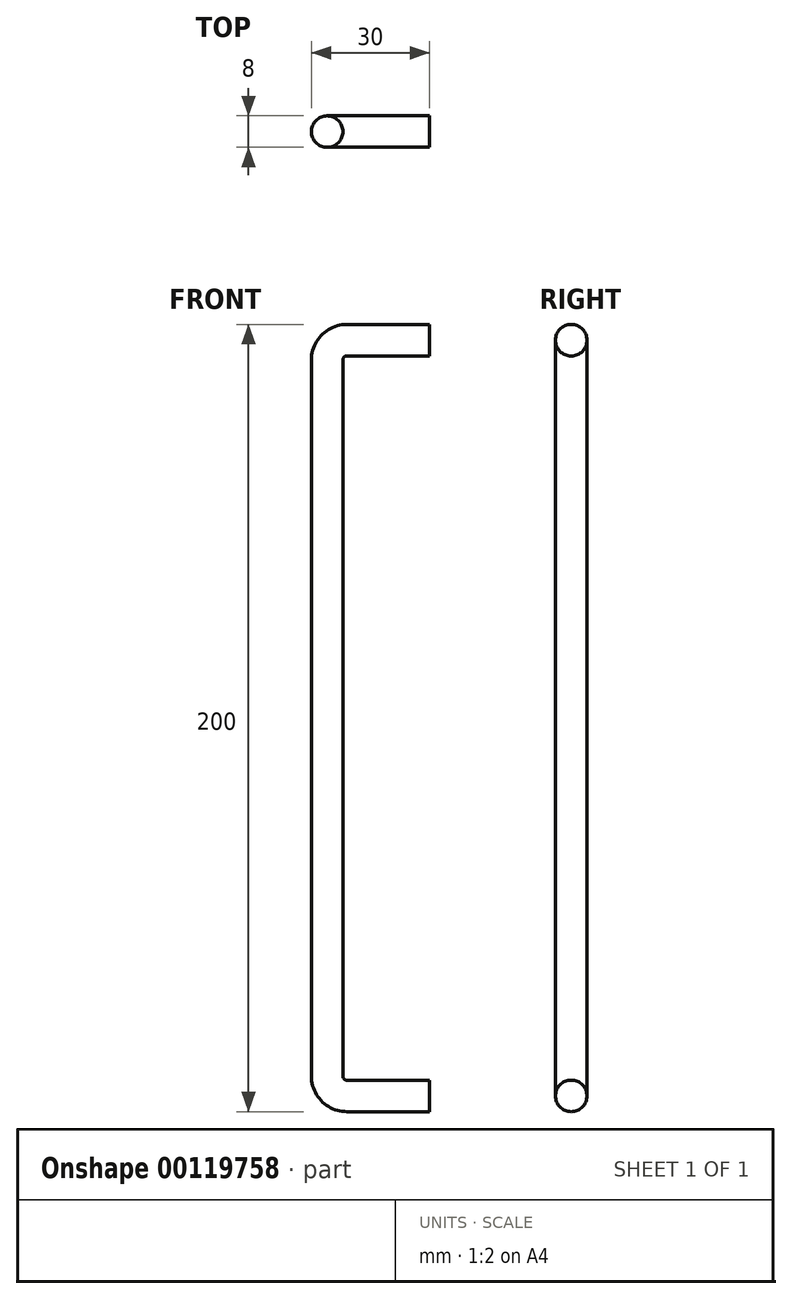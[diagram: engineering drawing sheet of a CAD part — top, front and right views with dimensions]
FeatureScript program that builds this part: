
annotation { "Feature Type Name" : "Feature", "Feature Type Description" : "" }
export const myFeature = defineFeature(function(context is Context, id is Id, definition is map)
    precondition{}
    {
        {
            var Q0;
            Q0=qCreatedBy(makeId("Front.planeOp"),FACE);
            var sketch = newSketch(context, id + "F0", { "sketchPlane" : qUnion([Q0])});
            skLineSegment(sketch, "E0", {"start": v(0, 0) * mm, "end": v(-21, 0) * mm});
            skLineSegment(sketch, "E1", {"start": v(-26, 5) * mm, "end": v(-26, 187) * mm});
            skLineSegment(sketch, "E2", {"start": v(-21, 192) * mm, "end": v(0, 192) * mm});
            skPoint(sketch, "E3.visualSharp", {"position": v(-26, 192) * mm});
            skArc(sketch, "E3.filletArc", {"start": v(-21, 192) * mm, "mid": v(-24.54, 190.54) * mm, "end": v(-26, 187) * mm});
            skPoint(sketch, "E4.visualSharp", {"position": v(-26, 0) * mm});
            skArc(sketch, "E4.filletArc", {"start": v(-26, 5) * mm, "mid": v(-24.54, 1.46) * mm, "end": v(-21, 0) * mm});
            skSolve(sketch);
        }
        {
            var Q0;
            Q0=qCreatedBy(makeId("Right.planeOp"),FACE);
            var sketch = newSketch(context, id + "F1", { "sketchPlane" : qUnion([Q0])});
            skCircle(sketch, "E5", {"center": v(0, 0) * mm, "radius": 4 * mm});
            skSolve(sketch);
        }
        {
            var Q0;
            Q0=makeQuery(id+"F1.imprint","IMPRINT",FACE,{"disambiguationData":[TD([[makeQuery(id+"F1.imprint","IMPRINT",EDGE,{"derivedFrom":sQuery(id+"F1.wireOp",EDGE,"E5")}),1.0]])]});
            var Q1;
            Q1=sQuery(id+"F0.wireOp",EDGE,"E0");
            var Q2;
            Q2=sQuery(id+"F0.wireOp",EDGE,"E4.filletArc");
            var Q3;
            Q3=sQuery(id+"F0.wireOp",EDGE,"E1");
            var Q4;
            Q4=sQuery(id+"F0.wireOp",EDGE,"E3.filletArc");
            var Q5;
            Q5=sQuery(id+"F0.wireOp",EDGE,"E2");
            sweep(context, id + "F2", {"profiles" : qUnion([Q0]), "path" : qUnion([Q1, Q2, Q3, Q4, Q5])});
        }
    });
